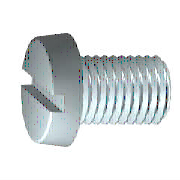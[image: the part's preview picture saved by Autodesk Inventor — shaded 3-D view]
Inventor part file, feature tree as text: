
AUTODESK INVENTOR PART (.ipt)
format: ipt  version: 2022 (Build 260153000, 153)  size: 186,880 bytes
history: native  units: mm (DEFAULTED — no unit token found)
features: sketch x2, other x1, extrude x1, plane x1
ambient origin geometry x7: Origin, YZ Plane, XZ Plane, X Axis, Y Axis, Z Axis, Center Point
bodies: Solid1 (feature_tree)
feature tree (5):
  other  "Базовый элемент"
  sketch  "Эскиз2"
  extrude  "Паз"  Depth=14.0mm
  plane  "Work Plane1"
  sketch  "Эскиз1"
